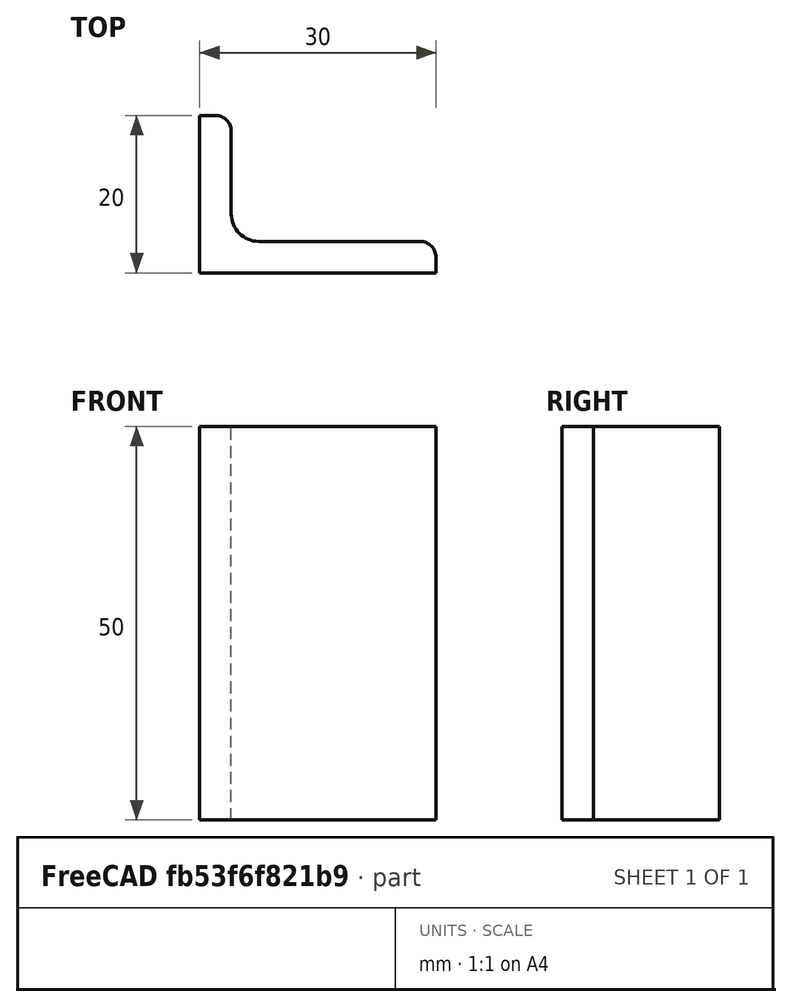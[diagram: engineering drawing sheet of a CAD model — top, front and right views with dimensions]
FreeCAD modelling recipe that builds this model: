
FCSTD DOCUMENT  (FreeCAD 0.15R4671 (Git))
Label: Angle Bar 30x20x4 EN10056 S235JR
License: All rights reserved
LicenseURL: http://en.wikipedia.org/wiki/All_rights_reserved
objects: Sketcher::SketchObject×1, Part::Extrusion×1
note: 2 computed .brp shape members not serialized (recipe doc carries the construction recipe); baked Part::Feature solids carry a one-line shape summary decoded from their .brp

FEATURE [Sketcher::SketchObject] Sketch
  sketch-geometry (9):
    g0: LineSegment StartX=0 StartY=0 StartZ=0 EndX=30 EndY=0 EndZ=0
    g1: LineSegment StartX=30 StartY=0 StartZ=0 EndX=30 EndY=2 EndZ=0
    g2: LineSegment StartX=28 StartY=4 StartZ=0 EndX=7.5 EndY=4 EndZ=0
    g3: LineSegment StartX=0 StartY=0 StartZ=0 EndX=0 EndY=20 EndZ=0
    g4: LineSegment StartX=0 StartY=20 StartZ=0 EndX=2 EndY=20 EndZ=0
    g5: LineSegment StartX=4 StartY=18 StartZ=0 EndX=4 EndY=7.5 EndZ=0
    g6: ArcOfCircle CenterX=7.5 CenterY=7.5 CenterZ=0 NormalX=0 NormalY=0 NormalZ=1 Radius=3.5 StartAngle=3.14159 EndAngle=4.71239
    g7: ArcOfCircle CenterX=2 CenterY=18 CenterZ=0 NormalX=0 NormalY=0 NormalZ=1 Radius=2 StartAngle=0 EndAngle=1.5708
    g8: ArcOfCircle CenterX=28 CenterY=2 CenterZ=0 NormalX=0 NormalY=0 NormalZ=1 Radius=2 StartAngle=0 EndAngle=1.5708
  constraints (23):
    c: Coincident(g0,g-1)
    c: Horizontal(g0)
    c: Coincident(g1,g0)
    c: Vertical(g1)
    c: Horizontal(g2)
    c: Coincident(g3,g-1)
    c: Vertical(g3)
    c: Coincident(g4,g3)
    c: Horizontal(g4)
    c: Vertical(g5)
    c: Tangent(g5,g6) = -1.5708
    c: Tangent(g2,g6) = 1.5708
    c: Tangent(g4,g7) = 1.5708
    c: Tangent(g5,g7) = 1.5708
    c: Tangent(g2,g8) = -1.5708
    c: Tangent(g1,g8) = -1.5708
    c: DistanceX(g0) = 30
    c: DistanceY(g3) = 20
    c: DistanceY(g0,g2) = 4
    c: DistanceX(g3,g5) = 4
    c: Radius(g6) = 3.5
    c: Radius(g8) = 2
    c: Radius(g7) = 2
FEATURE [Part::Extrusion] Extrude  label="Angle Bar 30x20x4 EN10056 S235JR"
  Base = -> Sketch
  Dir = (0,0,50)
  Solid = true
